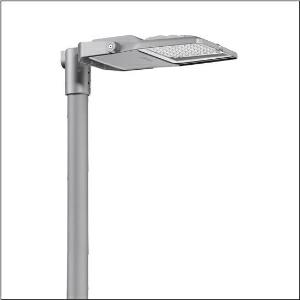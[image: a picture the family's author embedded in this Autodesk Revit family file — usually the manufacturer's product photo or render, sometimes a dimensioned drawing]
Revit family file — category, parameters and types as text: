
# Revit family: floodlight_fl_21_mini___pl33t_5xa7776b2f3a_1e67
name_source: partatom
category: Lighting Fixtures
units: mm (PartAtom-declared; Revit-internal decimal feet)

## family parameters
Cut with Voids When Loaded = No
Host = Face
Light Source = No
Part Type = Normal
Room Calculation Point = No
Round Connector Dimension = Use Diameter
Shared = No

## types (1)
- --- (1 x LED, 6150 lm, 45.7 W, 3000K)
    Apparent Load = 46 VA
    CIE Flux Codes = 26 75 99 100 100
    Color Rendering = 70
    Color Temperature = 3000K
    Default Elevation = 1800 mm
    Description = Floodlight FL 21 mini, floodlight, primary light control with lens, of PMMA, primary optical cover: protective disc, of toughened safety glass, transparent, light distribution: PL33T, light emission: direct distribution, installation type: surface-mounted, LED, High Power LED, rated luminous flux: 6.150lm, luminous efficacy: 135lm/W, light colour: 730, colour temperature: 3000K, control gear: Smart Interface (Zhaga), control: flexible luminous flux parameterisation, time-dependent luminous flux control, constant luminous flux control, overheat protection, pre-setting: logarithmic dimming characteristic, with terminal, 6-pole, mains connection: 220..240V, AC, 50/60Hz, start of lifetime: 46W, end of service life: 48W, reduction: 22W, luminaire housing, of diecast aluminium, powder-coated, Siteco® metallic grey (DB 702S), corrosivity category C5 mid according to DIN EN ISO 12944, suitable for swimming pools, chlorine-resistant, sealing non-destructively replaceable, please order mast flange separately, mast bracket, of steel, galvanised, powder-coated, Siteco® metallic grey (DB 702S), Smart Interface below and above, protection rating (complete): IP66, insulation class (complete): insulation class II (safety insulation), certification: CE, ENEC, VDE, protection symbol: D, impact resistance: IK08, permissible operating ambient temperature: -40..+40°C, permissible operating ambient temperature for outdoor applications: -40..+50°C, standard: DIN EN 12944, LABS conformity tested according to VDMA 24364:2018-05, packaging unit: 1 piece

Light Distribution: PL33T
    Height = 70 mm
    Lamp = 1 x LED
    Lamp Light Flux = 6150 lm
    Lamp Power = 45.7 W
    Lamp count = 1
    Length = 485 mm
    Luminous efficacy = 135 lm/W
    Manufacturer = Siteco
    ModVariant = No
    Model = 5XA7776B2F3A
    Number of Poles = 1
    OnlyDefault = Yes
    Power Factor = 1
    Product Name = Floodlight FL 21 mini | PL33T
    Product group = floodlight | pylon annexe
    ProductGroupID = 6200
    Protection Class = Protection class II
    Protection Degree = IP 66
    RLX_Detail_Level = 1
    RLX_Emergency_Light_Flux = 0 lm
    RLX_Emergency_Type = 0
    RLX_Emergency_Type_DB = No
    RlxData = <blob elided: 101009 chars, md5=0dba1eef>
    Socket = socket
    Standby Power = 0 W
    System Light Flux = 6150 lm
    System Power = 46 W
    Type Comments = factory setting: luminous flux: 100 % | dim-lin: 254 | 463 mA
    Type Image = l_1007125.jpg
    URL = http://relux.com
    VarID = @adj_144236
    Voltage = 0 V
    Weight = 0.00 kg
    Width = 337 mm

## geometry (parser evidence)
native form markers: Blend x4, Sweep x13
no freeform markers — native parametric forms only
